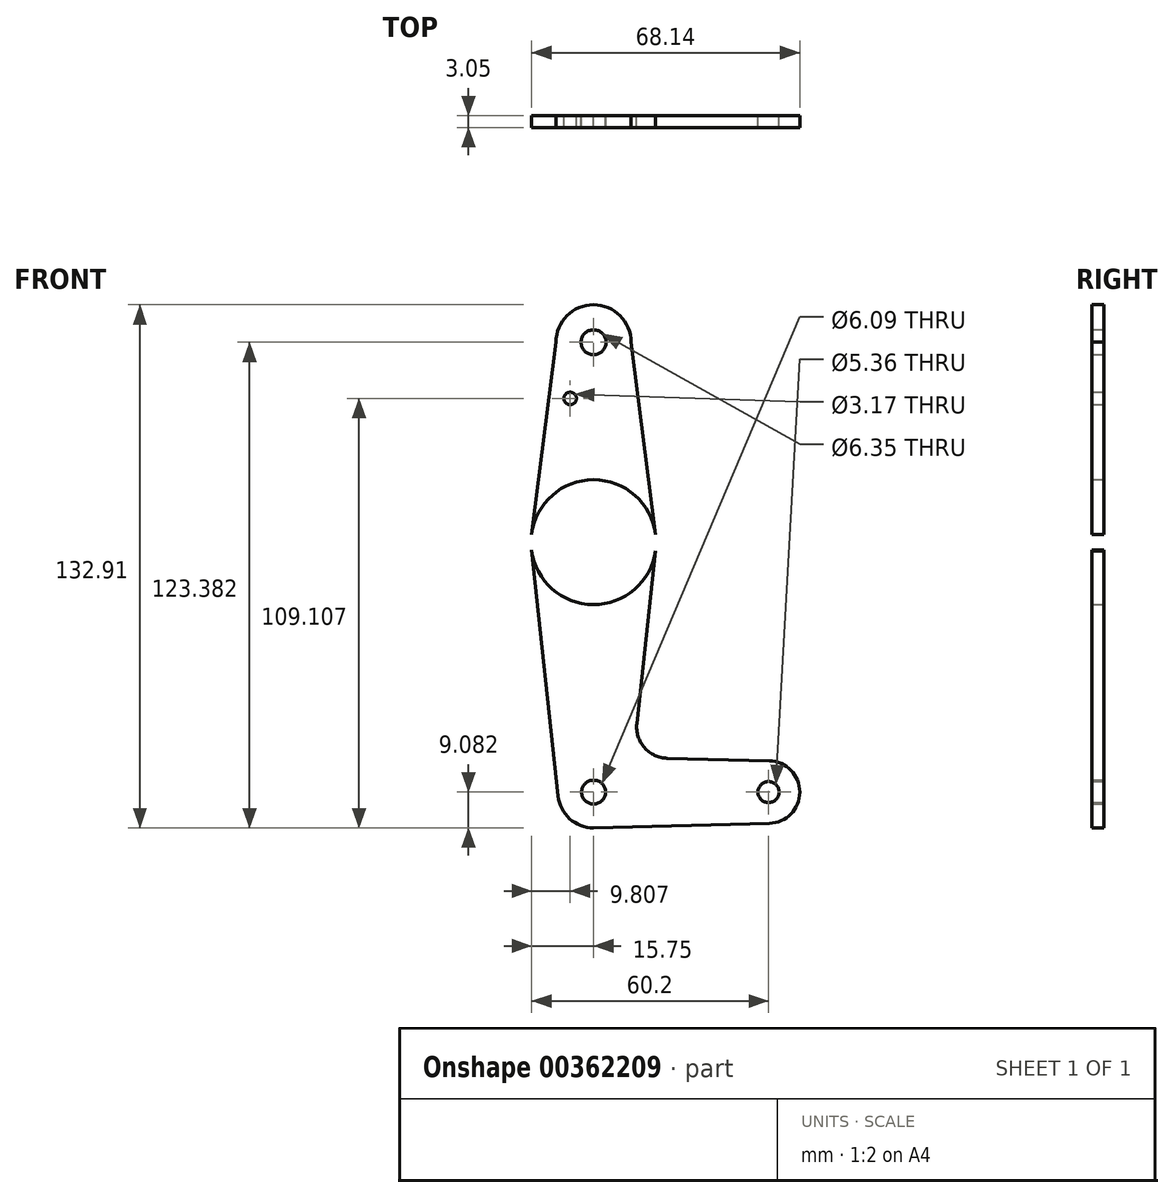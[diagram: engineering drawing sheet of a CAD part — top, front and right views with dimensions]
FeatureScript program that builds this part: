
annotation { "Feature Type Name" : "Feature", "Feature Type Description" : "" }
export const myFeature = defineFeature(function(context is Context, id is Id, definition is map)
    precondition{}
    {
        {
            var Q0;
            Q0=qCreatedBy(makeId("Front.planeOp"),FACE);
            var sketch = newSketch(context, id + "F0", { "sketchPlane" : qUnion([Q0])});
            skLineSegment(sketch, "E0", {"start": v(0, 73.08) * mm, "end": v(0, -41.22) * mm});
            skLineSegment(sketch, "E1", {"start": v(0, -41.22) * mm, "end": v(44.45, -41.22) * mm});
            skCircle(sketch, "E2", {"center": v(44.45, -41.22) * mm, "radius": 7.94 * mm});
            skCircle(sketch, "E3", {"center": v(0, 73.08) * mm, "radius": 9.53 * mm});
            skCircle(sketch, "E4", {"center": v(0, -41.22) * mm, "radius": 9.08 * mm});
            skCircle(sketch, "E5", {"center": v(0, 22.28) * mm, "radius": 15.88 * mm});
            skCircle(sketch, "E6", {"center": v(0, 73.08) * mm, "radius": 3.18 * mm});
            skCircle(sketch, "E7", {"center": v(0, 22.28) * mm, "radius": 3.49 * mm});
            skCircle(sketch, "E8", {"center": v(0, -41.22) * mm, "radius": 3.05 * mm});
            skCircle(sketch, "E9", {"center": v(44.45, -41.22) * mm, "radius": 2.68 * mm});
            skCircle(sketch, "E10", {"center": v(-5.94, 58.8) * mm, "radius": 1.59 * mm});
            skLineSegment(sketch, "E11", {"start": v(-9.52, 73.08) * mm, "end": v(-15.75, 24.3) * mm});
            skLineSegment(sketch, "E12", {"start": v(-15.75, 20.27) * mm, "end": v(-9.03, -42.19) * mm});
            skLineSegment(sketch, "E13", {"start": v(0, -50.3) * mm, "end": v(44.65, -49.15) * mm});
            skLineSegment(sketch, "E14", {"start": v(9.52, 73.08) * mm, "end": v(15.75, 24.3) * mm});
            skLineSegment(sketch, "E15", {"start": v(15.72, 20.07) * mm, "end": v(11, -23.82) * mm});
            skLineSegment(sketch, "E16", {"start": v(44.65, -33.28) * mm, "end": v(18.7, -32.62) * mm});
            skPoint(sketch, "E17.newPointA", {"position": v(9.03, -42.19) * mm});
            skPoint(sketch, "E17.newPointB", {"position": v(0, -32.14) * mm});
            skArc(sketch, "E17.filletArc", {"start": v(11, -23.82) * mm, "mid": v(12.92, -29.9) * mm, "end": v(18.7, -32.62) * mm});
            skSolve(sketch);
        }
        {
            var Q0;
            {var subQ0=sQuery(id+"F0.wireOp",EDGE,"E13");var subQ1=sQuery(id+"F0.wireOp",EDGE,"E4");var subQ2=makeQuery(id+"F0.imprint","INTERSECT",VERTEX,{"disambiguationData":[OD(0.0)],"derivedFrom":[subQ1,subQ0]});Q0=makeQuery(id+"F0.imprint","IMPRINT",FACE,{"disambiguationData":[TD([[makeQuery(id+"F0.imprint","IMPRINT",EDGE,{"disambiguationData":[TD([[subQ2,-1.0]])],"derivedFrom":subQ1}),1.0]])]});}
            var Q1;
            {var subQ5=sQuery(id+"F0.wireOp",EDGE,"E14");Q1=makeQuery(id+"F0.imprint","IMPRINT",FACE,{"disambiguationData":[TD([[makeQuery(id+"F0.imprint","IMPRINT",EDGE,{"derivedFrom":subQ5}),-1.0]])]});}
            var Q2;
            {var subQ0=sQuery(id+"F0.wireOp",EDGE,"E2");var subQ1=sQuery(id+"F0.wireOp",EDGE,"E1");var subQ2=makeQuery(id+"F0.imprint","INTERSECT",VERTEX,{"derivedFrom":[subQ1,subQ0]});Q2=makeQuery(id+"F0.imprint","IMPRINT",FACE,{"disambiguationData":[TD([[makeQuery(id+"F0.imprint","IMPRINT",EDGE,{"disambiguationData":[TD([[subQ2,1.0]])],"derivedFrom":subQ1}),-1.0]])]});}
            var Q3;
            Q3=makeQuery(id+"F0.imprint","IMPRINT",FACE,{"disambiguationData":[TD([[makeQuery(id+"F0.imprint","IMPRINT",EDGE,{"derivedFrom":sQuery(id+"F0.wireOp",EDGE,"E9")}),-1.0]])]});
            var Q4;
            Q4=makeQuery(id+"F0.imprint","IMPRINT",FACE,{"disambiguationData":[TD([[makeQuery(id+"F0.imprint","IMPRINT",EDGE,{"derivedFrom":sQuery(id+"F0.wireOp",EDGE,"E6")}),-1.0]])]});
            var Q5;
            Q5=makeQuery(id+"F0.imprint","IMPRINT",FACE,{"disambiguationData":[TD([[makeQuery(id+"F0.imprint","IMPRINT",EDGE,{"derivedFrom":sQuery(id+"F0.wireOp",EDGE,"E10")}),-1.0]])]});
            var Q6;
            {var subQ0=sQuery(id+"F0.wireOp",EDGE,"E5");var subQ2=sQuery(id+"F0.wireOp",EDGE,"E0");var subQ7=makeQuery(id+"F0.imprint","INTERSECT",VERTEX,{"disambiguationData":[OD(0.0)],"derivedFrom":[subQ2,subQ0]});Q6=makeQuery(id+"F0.imprint","IMPRINT",FACE,{"disambiguationData":[TD([[makeQuery(id+"F0.imprint","IMPRINT",EDGE,{"disambiguationData":[TD([[subQ7,-1.0]])],"derivedFrom":subQ2}),1.0]])]});}
            var Q7;
            {var subQ0=sQuery(id+"F0.wireOp",EDGE,"E5");var subQ2=sQuery(id+"F0.wireOp",EDGE,"E0");var subQ3=makeQuery(id+"F0.imprint","INTERSECT",VERTEX,{"disambiguationData":[OD(0.0)],"derivedFrom":[subQ2,subQ0]});Q7=makeQuery(id+"F0.imprint","IMPRINT",FACE,{"disambiguationData":[TD([[makeQuery(id+"F0.imprint","IMPRINT",EDGE,{"disambiguationData":[TD([[subQ3,-1.0]])],"derivedFrom":subQ2}),-1.0]])]});}
            var Q8;
            {var subQ10=sQuery(id+"F0.wireOp",EDGE,"E15");Q8=makeQuery(id+"F0.imprint","IMPRINT",FACE,{"disambiguationData":[TD([[makeQuery(id+"F0.imprint","IMPRINT",EDGE,{"derivedFrom":subQ10}),-1.0]])]});}
            var Q9;
            {var subQ0=sQuery(id+"F0.wireOp",EDGE,"E4");var subQ2=sQuery(id+"F0.wireOp",EDGE,"E0");var subQ3=makeQuery(id+"F0.imprint","INTERSECT",VERTEX,{"derivedFrom":[subQ2,subQ0]});Q9=makeQuery(id+"F0.imprint","IMPRINT",FACE,{"disambiguationData":[TD([[makeQuery(id+"F0.imprint","IMPRINT",EDGE,{"disambiguationData":[TD([[subQ3,-1.0]])],"derivedFrom":subQ2}),-1.0]])]});}
            var Q10;
            {var subQ5=sQuery(id+"F0.wireOp",EDGE,"E12");Q10=makeQuery(id+"F0.imprint","IMPRINT",FACE,{"disambiguationData":[TD([[makeQuery(id+"F0.imprint","IMPRINT",EDGE,{"derivedFrom":subQ5}),1.0]])]});}
            var Q11;
            {var subQ0=sQuery(id+"F0.wireOp",EDGE,"E4");var subQ1=sQuery(id+"F0.wireOp",EDGE,"E0");var subQ2=makeQuery(id+"F0.imprint","INTERSECT",VERTEX,{"derivedFrom":[subQ1,subQ0]});Q11=makeQuery(id+"F0.imprint","IMPRINT",FACE,{"disambiguationData":[TD([[makeQuery(id+"F0.imprint","IMPRINT",EDGE,{"disambiguationData":[TD([[subQ2,-1.0]])],"derivedFrom":subQ1}),1.0]])]});}
            extrude(context, id + "F1", {"entities" : qUnion([Q0, Q1, Q2, Q3, Q4, Q5, Q6, Q7, Q8, Q9, Q10, Q11]), "depth" : 3.05 * mm});
        }
    });
